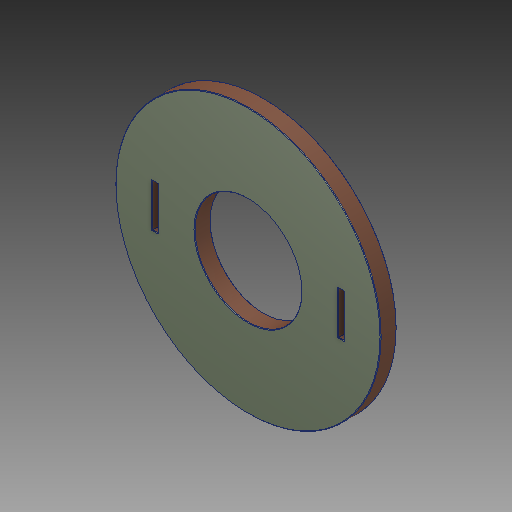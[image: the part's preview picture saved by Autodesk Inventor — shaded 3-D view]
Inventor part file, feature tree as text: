
AUTODESK INVENTOR PART (.ipt)
format: ipt  version: 2019 (Build 230136000, 136)  size: 143,360 bytes
history: mixed  units: mm
features: other x1, fillet x1, imported_body x1
ambient origin geometry x8: Origin, YZ Plane, XZ Plane, XY Plane, X Axis, Y Axis, Z Axis, Center Point
bodies: Body1 (imported_parasolid)
feature tree (3):
  other  "Твердое тело1"
  fillet  "Fillet1"  [1 undecoded]
  imported_body  NMx_Import_Brep_tag  [imported B-rep: ~32 faces, bbox_mm=[21.4, 4.1, 1.5]]
note: 1 required parameter value undecoded (feature->parameter linkage not recoverable at this tier; creation-order binding heuristic only, values carry confidence <= 0.55)
